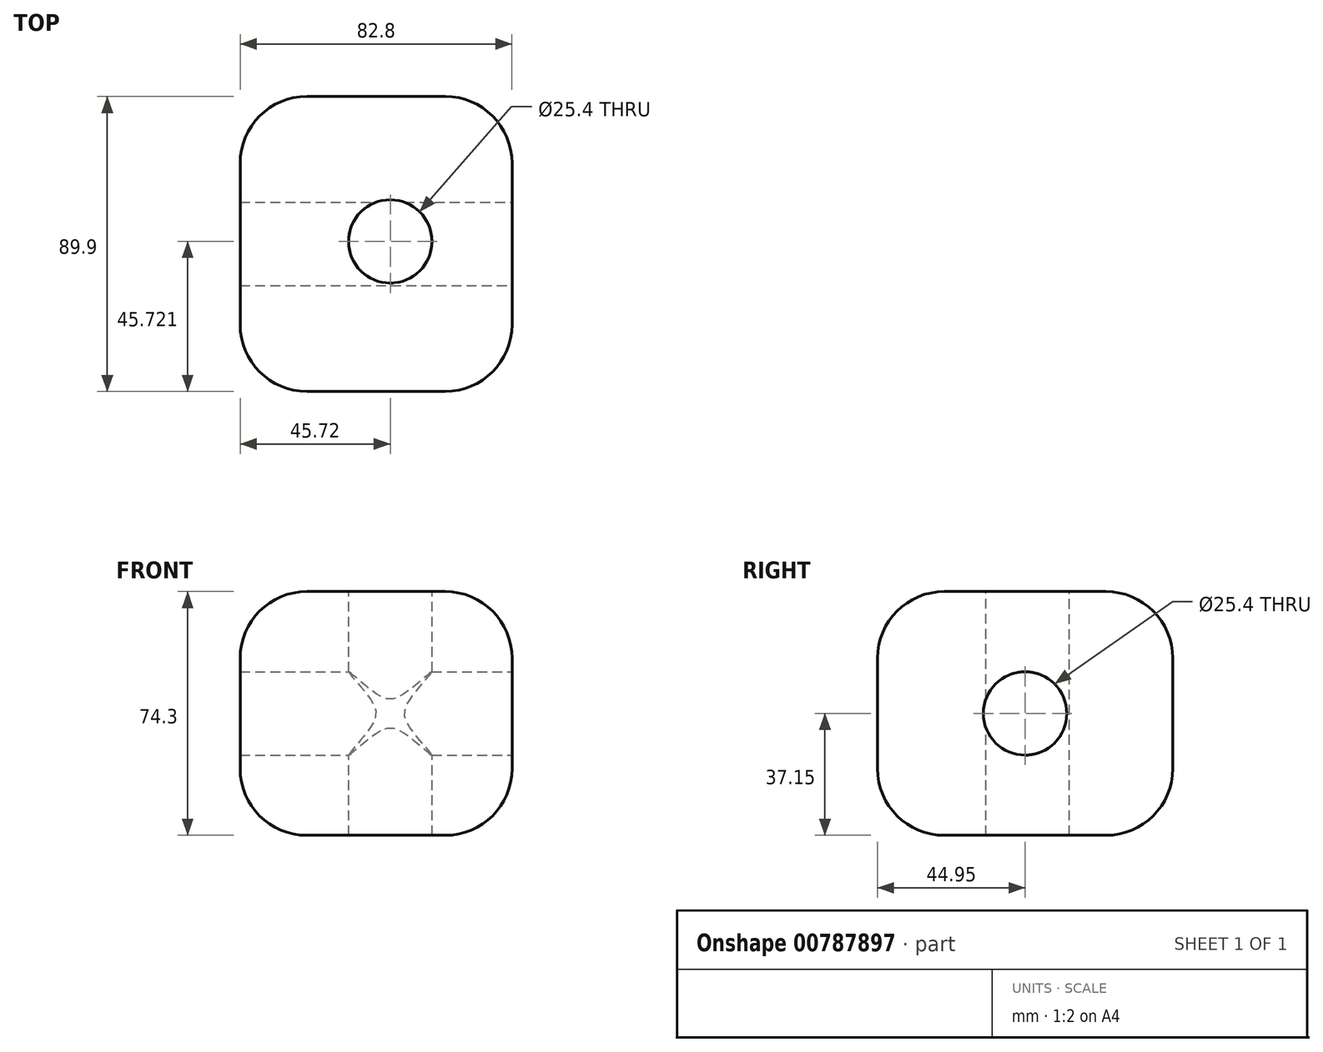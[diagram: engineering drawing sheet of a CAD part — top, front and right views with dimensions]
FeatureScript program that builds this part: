
annotation { "Feature Type Name" : "Feature", "Feature Type Description" : "" }
export const myFeature = defineFeature(function(context is Context, id is Id, definition is map)
    precondition{}
    {
        {
            var Q0;
            Q0=qCreatedBy(makeId("Right.planeOp"),FACE);
            var sketch = newSketch(context, id + "F0", { "sketchPlane" : qUnion([Q0])});
            skLineSegment(sketch, "E0.bottom", {"start": v(44.95, -37.15) * mm, "end": v(-44.95, -37.15) * mm});
            skLineSegment(sketch, "E0.top", {"start": v(44.95, 37.15) * mm, "end": v(-44.95, 37.15) * mm});
            skLineSegment(sketch, "E0.left", {"start": v(44.95, -37.15) * mm, "end": v(44.95, 37.15) * mm});
            skLineSegment(sketch, "E0.right", {"start": v(-44.95, -37.15) * mm, "end": v(-44.95, 37.15) * mm});
            skPoint(sketch, "E0.middle", {"position": v(0, 0) * mm});
            skSolve(sketch);
        }
        {
            var Q0;
            Q0=makeQuery(id+"F0.imprint","IMPRINT",FACE,{"disambiguationData":[TD([[makeQuery(id+"F0.imprint","IMPRINT",EDGE,{"derivedFrom":sQuery(id+"F0.wireOp",EDGE,"E0.bottom")}),-1.0]])]});
            extrude(context, id + "F1", {"entities" : qUnion([Q0]), "depth" : 82.8 * mm, "offsetDistance" : 25.4 * mm});
        }
        {
            var Q0;
            Q0=makeQuery(id+"F1.opExtrude","SWEPT_FACE",FACE,{"disambiguationData":[OSD([sQuery(id+"F0.wireOp",EDGE,"E0.top")])]});
            var Q1;
            Q1=makeQuery(id+"F1.opExtrude","CAP_FACE",FACE,{"disambiguationData":[OSD([sQuery(id+"F0.wireOp",EDGE,"E0.bottom"),sQuery(id+"F0.wireOp",EDGE,"E0.top"),sQuery(id+"F0.wireOp",EDGE,"E0.left"),sQuery(id+"F0.wireOp",EDGE,"E0.right")])],"isStart":false});
            var Q2;
            Q2=makeQuery(id+"F1.opExtrude","SWEPT_FACE",FACE,{"disambiguationData":[OSD([sQuery(id+"F0.wireOp",EDGE,"E0.right")])]});
            var Q3;
            Q3=makeQuery(id+"F1.opExtrude","SWEPT_FACE",FACE,{"disambiguationData":[OSD([sQuery(id+"F0.wireOp",EDGE,"E0.left")])]});
            var Q4;
            Q4=makeQuery(id+"F1.opExtrude","CAP_FACE",FACE,{"disambiguationData":[OSD([sQuery(id+"F0.wireOp",EDGE,"E0.bottom"),sQuery(id+"F0.wireOp",EDGE,"E0.top"),sQuery(id+"F0.wireOp",EDGE,"E0.left"),sQuery(id+"F0.wireOp",EDGE,"E0.right")])],"isStart":true});
            var Q5;
            Q5=makeQuery(id+"F1.opExtrude","SWEPT_FACE",FACE,{"disambiguationData":[OSD([sQuery(id+"F0.wireOp",EDGE,"E0.bottom")])]});
            fillet(context, id + "F2", {"entities" : qUnion([Q0, Q1, Q2, Q3, Q4, Q5]), "radius" : 20.32 * mm, "tangentPropagation" : true, "allowEdgeOverflow" : false});
        }
        {
            var Q0;
            Q0=makeQuery(id+"F1.opExtrude","SWEPT_FACE",FACE,{"disambiguationData":[OSD([sQuery(id+"F0.wireOp",EDGE,"E0.top")])]});
            var sketch = newSketch(context, id + "F3", { "sketchPlane" : qUnion([Q0])});
            skPoint(sketch, "E1", {"position": v(45.72, 0.77) * mm});
            skSolve(sketch);
        }
        {
            var Q0;
            Q0=sQuery(id+"F3.wireOp",VERTEX,"E1");
            var Q1;
            Q1=makeQuery(id+"F1.opExtrude","SWEPT_BODY",BODY,{"disambiguationData":[OSD([sQuery(id+"F0.wireOp",EDGE,"E0.bottom"),sQuery(id+"F0.wireOp",EDGE,"E0.top"),sQuery(id+"F0.wireOp",EDGE,"E0.left"),sQuery(id+"F0.wireOp",EDGE,"E0.right")])]});
            hole(context, id + "F4", {"style" : HoleStyle.SIMPLE, "endStyle" : HoleEndStyle.THROUGH, "holeDiameter" : 25.4 * mm, "majorDiameter" : 6.35 * mm, "isTappedThrough" : true, "tappedDepth" : 12.7 * mm, "tapClearance" : 3, "locations" : qUnion([Q0]), "scope" : qUnion([Q1])});
        }
        {
            var Q0;
            Q0=makeQuery(id+"F1.opExtrude","CAP_FACE",FACE,{"disambiguationData":[OSD([sQuery(id+"F0.wireOp",EDGE,"E0.bottom"),sQuery(id+"F0.wireOp",EDGE,"E0.top"),sQuery(id+"F0.wireOp",EDGE,"E0.left"),sQuery(id+"F0.wireOp",EDGE,"E0.right")])],"isStart":false});
            var sketch = newSketch(context, id + "F5", { "sketchPlane" : qUnion([Q0])});
            skCircle(sketch, "E2", {"center": v(0, 0) * mm, "radius": 11.37 * mm});
            skSolve(sketch);
        }
        {
            var Q0;
            Q0=sQuery(id+"F5.wireOp",VERTEX,"E2.center");
            var Q1;
            Q1=makeQuery(id+"F1.opExtrude","SWEPT_BODY",BODY,{"disambiguationData":[OSD([sQuery(id+"F0.wireOp",EDGE,"E0.bottom"),sQuery(id+"F0.wireOp",EDGE,"E0.top"),sQuery(id+"F0.wireOp",EDGE,"E0.left"),sQuery(id+"F0.wireOp",EDGE,"E0.right")])]});
            hole(context, id + "F6", {"style" : HoleStyle.SIMPLE, "endStyle" : HoleEndStyle.THROUGH, "holeDiameter" : 25.4 * mm, "majorDiameter" : 6.35 * mm, "isTappedThrough" : true, "tappedDepth" : 12.7 * mm, "tapClearance" : 3, "locations" : qUnion([Q0]), "scope" : qUnion([Q1])});
        }
    });
